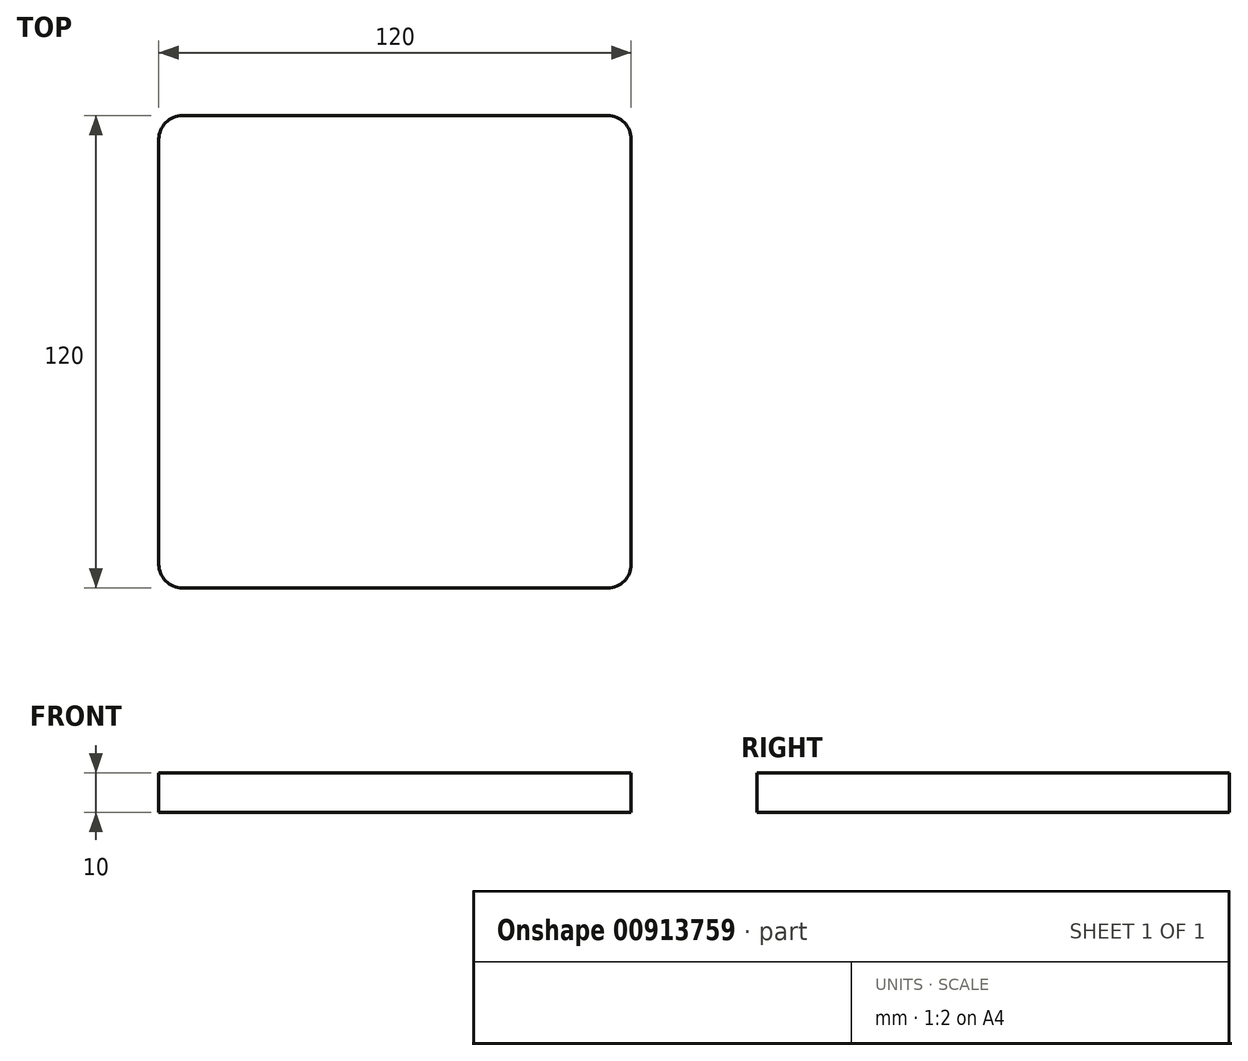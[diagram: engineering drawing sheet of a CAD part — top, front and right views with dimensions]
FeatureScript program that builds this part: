
annotation { "Feature Type Name" : "Feature", "Feature Type Description" : "" }
export const myFeature = defineFeature(function(context is Context, id is Id, definition is map)
    precondition{}
    {
        {
            var Q0;
            Q0=qCreatedBy(makeId("Top.planeOp"),FACE);
            var sketch = newSketch(context, id + "F0", { "sketchPlane" : qUnion([Q0])});
            skLineSegment(sketch, "E0.bottom", {"start": v(54, -60) * mm, "end": v(-54, -60) * mm});
            skLineSegment(sketch, "E0.top", {"start": v(54, 60) * mm, "end": v(-54, 60) * mm});
            skLineSegment(sketch, "E0.left", {"start": v(60, -54) * mm, "end": v(60, 54) * mm});
            skLineSegment(sketch, "E0.right", {"start": v(-60, -54) * mm, "end": v(-60, 54) * mm});
            skPoint(sketch, "E0.middle", {"position": v(0, 0) * mm});
            skPoint(sketch, "E1.visualSharp", {"position": v(-60, 60) * mm});
            skArc(sketch, "E1.filletArc", {"start": v(-54, 60) * mm, "mid": v(-58.24, 58.24) * mm, "end": v(-60, 54) * mm});
            skPoint(sketch, "E2.visualSharp", {"position": v(60, 60) * mm});
            skArc(sketch, "E2.filletArc", {"start": v(60, 54) * mm, "mid": v(58.24, 58.24) * mm, "end": v(54, 60) * mm});
            skPoint(sketch, "E3.visualSharp", {"position": v(60, -60) * mm});
            skArc(sketch, "E3.filletArc", {"start": v(54, -60) * mm, "mid": v(58.24, -58.24) * mm, "end": v(60, -54) * mm});
            skPoint(sketch, "E4.visualSharp", {"position": v(-60, -60) * mm});
            skArc(sketch, "E4.filletArc", {"start": v(-60, -54) * mm, "mid": v(-58.24, -58.24) * mm, "end": v(-54, -60) * mm});
            skSolve(sketch);
        }
        {
            var Q0;
            Q0 = qSketchRegion(id + "F0", true);
            extrude(context, id + "F1", {"entities" : qUnion([Q0]), "depth" : 10 * mm, "offsetDistance" : 25.4 * mm});
        }
    });
